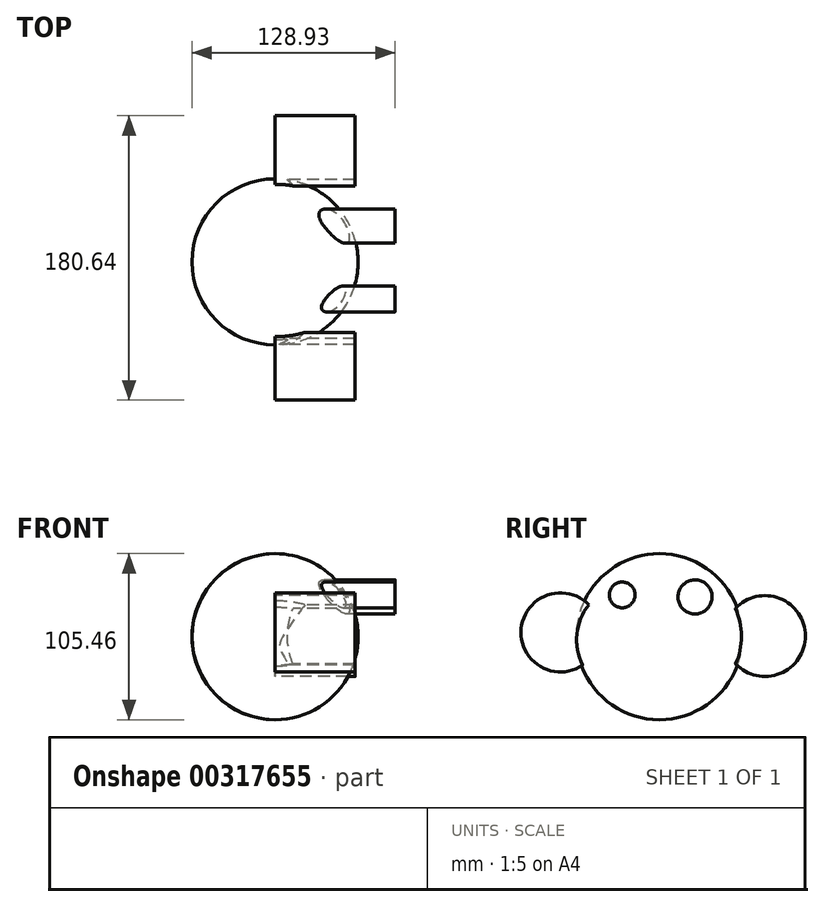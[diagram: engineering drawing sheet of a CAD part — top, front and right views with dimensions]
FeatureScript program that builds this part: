
annotation { "Feature Type Name" : "Feature", "Feature Type Description" : "" }
export const myFeature = defineFeature(function(context is Context, id is Id, definition is map)
    precondition{}
    {
        {
            var Q0;
            Q0=qCreatedBy(makeId("Right.planeOp"),FACE);
            var sketch = newSketch(context, id + "F0", { "sketchPlane" : qUnion([Q0])});
            skCircle(sketch, "E0", {"center": v(0, 0) * mm, "radius": 52.73 * mm});
            skLineSegment(sketch, "E1", {"start": v(0, 52.73) * mm, "end": v(0, -52.73) * mm});
            skSolve(sketch);
        }
        {
            var Q0;
            {var subQ0=sQuery(id+"F0.wireOp",EDGE,"E1");Q0=makeQuery(id+"F0.imprint","IMPRINT",FACE,{"disambiguationData":[TD([[makeQuery(id+"F0.imprint","IMPRINT",EDGE,{"derivedFrom":subQ0}),1.0]])]});}
            var Q1;
            Q1=sQuery(id+"F0.wireOp",EDGE,"E1");
            revolve(context, id + "F1", {"entities" : qUnion([Q0]), "axis" : qUnion([Q1]), "revolveType" : RevolveType.FULL});
        }
        {
            var Q0;
            Q0=qCreatedBy(makeId("Right.planeOp"),FACE);
            var sketch = newSketch(context, id + "F2", { "sketchPlane" : qUnion([Q0])});
            skCircle(sketch, "E2", {"center": v(-23.6, 26.55) * mm, "radius": 8.16 * mm});
            skCircle(sketch, "E3", {"center": v(22.68, 25.26) * mm, "radius": 10.84 * mm});
            skArc(sketch, "E4", {"start": v(-44.8, 20.28) * mm, "mid": v(-87.74, 5.25) * mm, "end": v(-48.67, -18.07) * mm});
            skArc(sketch, "E5", {"start": v(48.49, -17.33) * mm, "mid": v(92.77, 0.5) * mm, "end": v(48.3, 17.88) * mm});
            skArc(sketch, "E6", {"start": v(-24.15, -11.43) * mm, "mid": v(2.77, -50.33) * mm, "end": v(29.68, -11.43) * mm});
            skArc(sketch, "E7", {"start": v(48.49, -17.33) * mm, "mid": v(52.15, 0.3) * mm, "end": v(48.3, 17.88) * mm});
            skArc(sketch, "E8", {"start": v(-44.8, 20.28) * mm, "mid": v(-52.37, 1.67) * mm, "end": v(-48.67, -18.07) * mm});
            skSolve(sketch);
        }
        {
            var Q0;
            Q0 = qSketchRegion(id + "F2", true);
            extrude(context, id + "F3", {"entities" : qUnion([Q0]), "operationType" : NewBodyOperationType.ADD, "depth" : 50.8 * mm});
        }
        {
            var Q0;
            Q0=makeQuery(id+"F3.opExtrude","CAP_FACE",FACE,{"disambiguationData":[OSD([sQuery(id+"F2.wireOp",EDGE,"E2")])],"isStart":false});
            var Q1;
            Q1=makeQuery(id+"F3.opExtrude","CAP_FACE",FACE,{"disambiguationData":[OSD([sQuery(id+"F2.wireOp",EDGE,"E3")])],"isStart":false});
            extrude(context, id + "F4", {"entities" : qUnion([Q0, Q1]), "operationType" : NewBodyOperationType.ADD, "depth" : 25.4 * mm});
        }
        {
            var Q0;
            Q0=qCreatedBy(makeId("Right.planeOp"),FACE);
            var sketch = newSketch(context, id + "F5", { "sketchPlane" : qUnion([Q0])});
            skLineSegment(sketch, "E9", {"start": v(-34.43, -32.63) * mm, "end": v(-34.43, -67.66) * mm});
            skLineSegment(sketch, "E10", {"start": v(-13.96, -36.5) * mm, "end": v(-13.96, -68.95) * mm});
            skLineSegment(sketch, "E11", {"start": v(18.11, -35.21) * mm, "end": v(16.27, -69.5) * mm});
            skLineSegment(sketch, "E12", {"start": v(31.2, -34.84) * mm, "end": v(31.2, -68.21) * mm});
            skLineSegment(sketch, "E13", {"start": v(31.2, -68.21) * mm, "end": v(16.27, -69.5) * mm});
            skLineSegment(sketch, "E14", {"start": v(-13.96, -68.95) * mm, "end": v(-34.43, -67.66) * mm});
            skLineSegment(sketch, "E15", {"start": v(-34.43, -32.63) * mm, "end": v(-28.53, -32.63) * mm});
            skLineSegment(sketch, "E16", {"start": v(-13.96, -36.5) * mm, "end": v(-28.53, -32.63) * mm});
            skLineSegment(sketch, "E17", {"start": v(18.11, -35.21) * mm, "end": v(31.2, -34.84) * mm});
            skSolve(sketch);
        }
    });
